# Revit family: QF_Summit_ACK54COILW_Kitchenette_with_Range_Refrigerator_Freezer
name_source: partatom
category: Specialty Equipment
units: mm (PartAtom-declared; Revit-internal decimal feet)

## family parameters
Always vertical = Yes
Cut with Voids When Loaded = No
Part Type = Normal
Room Calculation Point = No
Round Connector Dimension = Use Diameter
Shared = No
Work Plane-Based = No

## types (1)
- QF_Summit_ACK54COILW_Kitchenette_with_Range_Refrigerator_Freezer
    Apparent Power = 8800 VA
    BTUH = 0.0 Btu/h
    Conn Conduit = Yes
    Cycle = 60 Hz
    Default Elevation = 0"
    Depth = 23 3/4"
    Description = Kichenette with Range & Refrigerator/Freezer
    Elec Conn Connection Height = 0"
    Elec Conn RI Height = 0"
    Electrical Remarks = 40 amps Range; 1.1 amp refrigerator
    FL Amps = 40 A
    Foodservice Equipment Identifier = Yes
    Height = 42"
    Identify Quantity as Lot = Yes
    Length = 53 1/2"
    Manufacturer = Summit
    Max Overcurrent Protection = 0 A
    Min Ckt Ampacity = 0 A
    Model = ACK54COILW
    Number of Poles = 1
    Phase = 1
    Refrigerant Type = R600a
    Refrigerant Volume = 0.00 kip
    Volts = 220 V
    Watts = 8800 W
    Weight in Pounds = 253

## geometry (parser evidence)
native form markers: Blend x2, Sweep x13
no freeform markers — native parametric forms only
